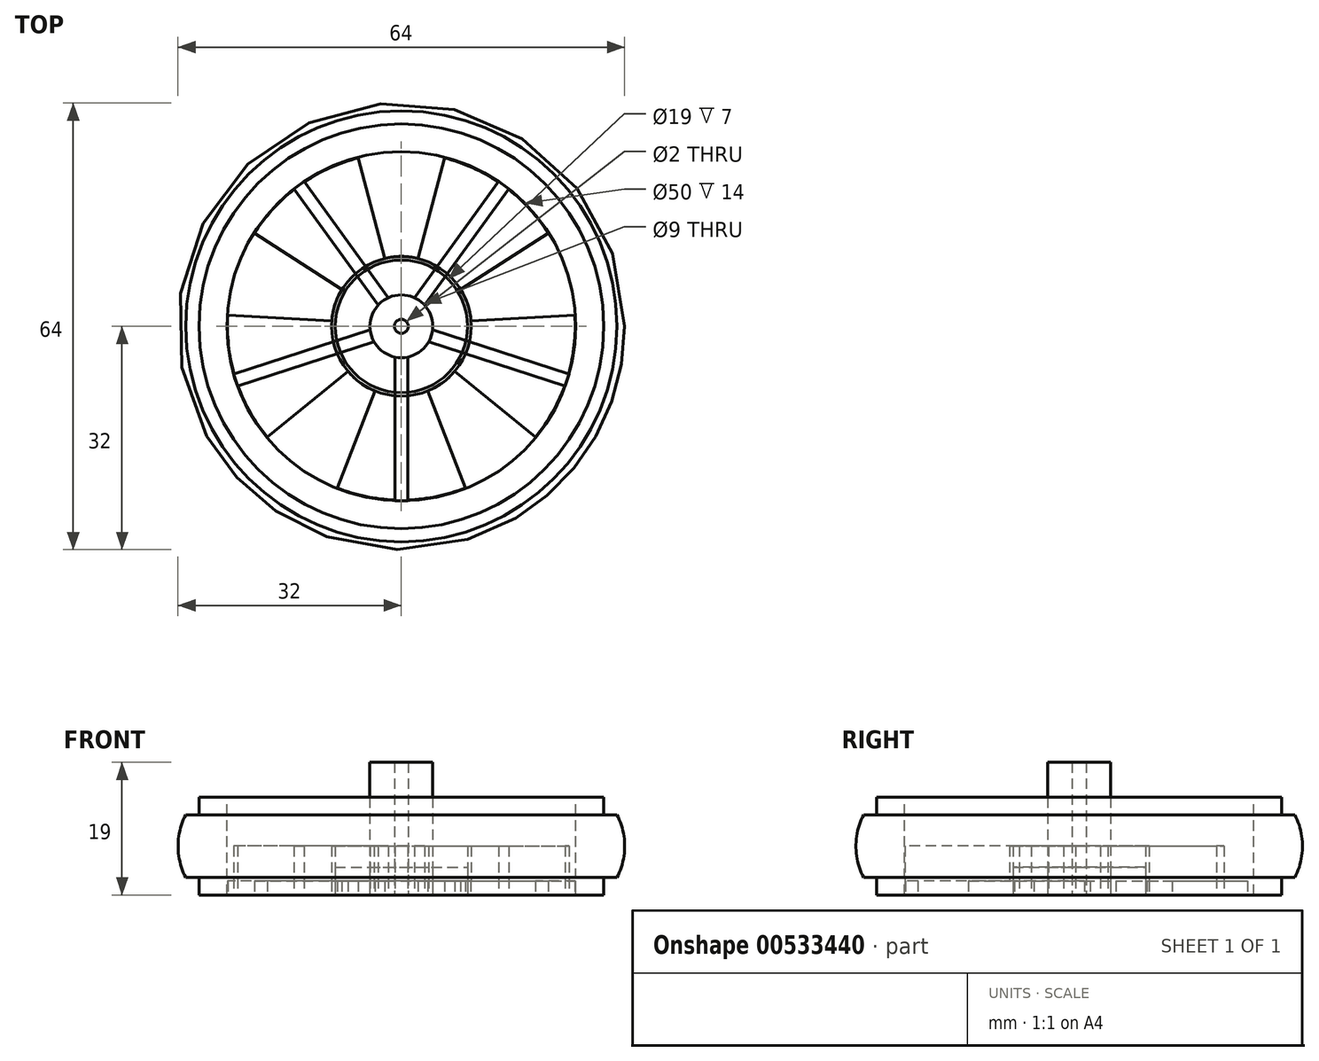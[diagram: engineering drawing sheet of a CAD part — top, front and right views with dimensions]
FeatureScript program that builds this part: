
annotation { "Feature Type Name" : "Feature", "Feature Type Description" : "" }
export const myFeature = defineFeature(function(context is Context, id is Id, definition is map)
    precondition{}
    {
        {
            var Q0;
            Q0=qCreatedBy(makeId("Front.planeOp"),FACE);
            var sketch = newSketch(context, id + "F0", { "sketchPlane" : qUnion([Q0])});
            skLineSegment(sketch, "E0", {"start": v(0, 0) * mm, "end": v(25, 0) * mm});
            skLineSegment(sketch, "E1", {"start": v(25, 0) * mm, "end": v(25, 14) * mm});
            skLineSegment(sketch, "E2", {"start": v(25, 14) * mm, "end": v(29, 14) * mm});
            skLineSegment(sketch, "E3", {"start": v(25, 0) * mm, "end": v(29, 0) * mm});
            skArc(sketch, "E4", {"start": v(30.89, 2.5) * mm, "mid": v(32, 7) * mm, "end": v(30.89, 11.5) * mm});
            skLineSegment(sketch, "E5", {"start": v(0, 2) * mm, "end": v(25, 2) * mm});
            skLineSegment(sketch, "E6", {"start": v(0, 30.9) * mm, "end": v(0, -20.2) * mm, "construction": true});
            skLineSegment(sketch, "E7", {"start": v(29, 14) * mm, "end": v(29, 11.5) * mm});
            skLineSegment(sketch, "E8", {"start": v(29, 11.5) * mm, "end": v(30.89, 11.5) * mm});
            skLineSegment(sketch, "E9", {"start": v(29, 0) * mm, "end": v(29, 2.5) * mm});
            skLineSegment(sketch, "E10", {"start": v(29, 2.5) * mm, "end": v(30.89, 2.5) * mm});
            skSolve(sketch);
        }
        {
            var Q0;
            {var subQ1=sQuery(id+"F0.wireOp",EDGE,"E2");Q0=makeQuery(id+"F0.imprint","IMPRINT",FACE,{"disambiguationData":[TD([[makeQuery(id+"F0.imprint","IMPRINT",EDGE,{"derivedFrom":subQ1}),-1.0]])]});}
            var Q1;
            Q1=sQuery(id+"F0.wireOp",EDGE,"E6");
            revolve(context, id + "F1", {"entities" : qUnion([Q0]), "axis" : qUnion([Q1]), "revolveType" : RevolveType.FULL});
        }
        {
            var Q0;
            Q0=makeQuery(id+"F1.opRevolve","SWEPT_FACE",FACE,{"disambiguationData":[OSD([sQuery(id+"F0.wireOp",EDGE,"E3")])]});
            var sketch = newSketch(context, id + "F2", { "sketchPlane" : qUnion([Q0])});
            skCircle(sketch, "E11", {"center": v(0, 0) * mm, "radius": 24.91 * mm});
            skCircle(sketch, "E12", {"center": v(0, 0) * mm, "radius": 4.5 * mm});
            skCircle(sketch, "E13", {"center": v(0, 0) * mm, "radius": 1 * mm});
            skCircle(sketch, "E14", {"center": v(0, 0) * mm, "radius": 9.5 * mm});
            skCircle(sketch, "E15", {"center": v(0, 0) * mm, "radius": 10 * mm});
            skSolve(sketch);
        }
        {
            var Q0;
            Q0 = qSketchRegion(id + "F2", true);
            extrude(context, id + "F3", {"entities" : qUnion([Q0]), "oppositeDirection" : true, "depth" : 2 * mm, "offsetDistance" : 25 * mm});
        }
        {
            var Q0;
            Q0=makeQuery(id+"F2.imprint","IMPRINT",FACE,{"disambiguationData":[TD([[makeQuery(id+"F2.imprint","IMPRINT",EDGE,{"derivedFrom":sQuery(id+"F2.wireOp",EDGE,"E12")}),1.0]])]});
            extrude(context, id + "F4", {"entities" : qUnion([Q0]), "oppositeDirection" : true, "depth" : 19 * mm, "offsetDistance" : 25 * mm});
        }
        {
            var Q0;
            Q0=makeQuery(id+"F2.imprint","IMPRINT",FACE,{"disambiguationData":[TD([[makeQuery(id+"F2.imprint","IMPRINT",EDGE,{"derivedFrom":sQuery(id+"F2.wireOp",EDGE,"E14")}),-1.0]])]});
            extrude(context, id + "F5", {"entities" : qUnion([Q0]), "operationType" : NewBodyOperationType.ADD, "oppositeDirection" : true, "depth" : 7 * mm, "offsetDistance" : 25 * mm});
        }
        {
            var Q0;
            Q0=makeQuery(id+"F2.imprint","IMPRINT",FACE,{"disambiguationData":[TD([[makeQuery(id+"F2.imprint","IMPRINT",EDGE,{"derivedFrom":sQuery(id+"F2.wireOp",EDGE,"E12")}),-1.0]])]});
            extrude(context, id + "F6", {"entities" : qUnion([Q0]), "oppositeDirection" : true, "depth" : 4 * mm, "offsetDistance" : 25 * mm});
        }
        {
            var Q0;
            Q0=qCreatedBy(makeId("Top.planeOp"),FACE);
            var sketch = newSketch(context, id + "F7", { "sketchPlane" : qUnion([Q0])});
            skLineSegment(sketch, "E16.bottom", {"start": v(0, -4.4) * mm, "end": v(-0.9, -4.4) * mm});
            skLineSegment(sketch, "E16.top", {"start": v(0, -24.98) * mm, "end": v(-0.9, -24.98) * mm});
            skLineSegment(sketch, "E16.right", {"start": v(-0.9, -4.4) * mm, "end": v(-0.9, -24.98) * mm});
            skLineSegment(sketch, "E17.MirrorCS", {"start": v(0.9, -4.4) * mm, "end": v(0.9, -24.98) * mm});
            skLineSegment(sketch, "E18", {"start": v(0, -24.98) * mm, "end": v(0.9, -24.98) * mm});
            skLineSegment(sketch, "E19", {"start": v(0, -4.4) * mm, "end": v(0.9, -4.4) * mm});
            skLineSegment(sketch, "E20.1.0", {"start": v(3.91, -2.23) * mm, "end": v(23.48, -8.58) * mm});
            skLineSegment(sketch, "E20.1.1", {"start": v(4.47, -0.5) * mm, "end": v(24.04, -6.86) * mm});
            skLineSegment(sketch, "E20.1.2", {"start": v(4.2, -1.36) * mm, "end": v(4.47, -0.5) * mm});
            skLineSegment(sketch, "E20.1.3", {"start": v(4.2, -1.36) * mm, "end": v(3.91, -2.23) * mm});
            skLineSegment(sketch, "E20.1.4", {"start": v(23.76, -7.72) * mm, "end": v(24.04, -6.86) * mm});
            skLineSegment(sketch, "E20.1.5", {"start": v(23.76, -7.72) * mm, "end": v(23.48, -8.58) * mm});
            skLineSegment(sketch, "E20.2.0", {"start": v(3.33, 3.03) * mm, "end": v(15.42, 19.68) * mm});
            skLineSegment(sketch, "E20.2.1", {"start": v(1.86, 4.1) * mm, "end": v(13.95, 20.75) * mm});
            skLineSegment(sketch, "E20.2.2", {"start": v(2.6, 3.57) * mm, "end": v(1.86, 4.1) * mm});
            skLineSegment(sketch, "E20.2.3", {"start": v(2.6, 3.57) * mm, "end": v(3.33, 3.03) * mm});
            skLineSegment(sketch, "E20.2.4", {"start": v(14.68, 20.21) * mm, "end": v(13.95, 20.75) * mm});
            skLineSegment(sketch, "E20.2.5", {"start": v(14.68, 20.21) * mm, "end": v(15.42, 19.68) * mm});
            skPoint(sketch, "E20.center", {"position": v(0, 0) * mm});
            skLineSegment(sketch, "E21.2.3.0", {"start": v(-1.86, 4.1) * mm, "end": v(-13.95, 20.75) * mm});
            skLineSegment(sketch, "E21.3.3.0", {"start": v(-3.33, 3.03) * mm, "end": v(-15.42, 19.68) * mm});
            skLineSegment(sketch, "E21.6.3.0", {"start": v(-2.6, 3.57) * mm, "end": v(-3.33, 3.03) * mm});
            skLineSegment(sketch, "E21.9.3.0", {"start": v(-2.6, 3.57) * mm, "end": v(-1.86, 4.1) * mm});
            skLineSegment(sketch, "E21.12.3.0", {"start": v(-14.68, 20.21) * mm, "end": v(-15.42, 19.68) * mm});
            skLineSegment(sketch, "E21.15.3.0", {"start": v(-14.68, 20.21) * mm, "end": v(-13.95, 20.75) * mm});
            skLineSegment(sketch, "E21.2.4.0", {"start": v(-4.47, -0.5) * mm, "end": v(-24.04, -6.86) * mm});
            skLineSegment(sketch, "E21.3.4.0", {"start": v(-3.91, -2.23) * mm, "end": v(-23.48, -8.58) * mm});
            skLineSegment(sketch, "E21.6.4.0", {"start": v(-4.2, -1.36) * mm, "end": v(-3.91, -2.23) * mm});
            skLineSegment(sketch, "E21.9.4.0", {"start": v(-4.2, -1.36) * mm, "end": v(-4.47, -0.5) * mm});
            skLineSegment(sketch, "E21.12.4.0", {"start": v(-23.76, -7.72) * mm, "end": v(-23.48, -8.58) * mm});
            skLineSegment(sketch, "E21.15.4.0", {"start": v(-23.76, -7.72) * mm, "end": v(-24.04, -6.86) * mm});
            skSolve(sketch);
        }
        {
            var Q0;
            Q0=makeQuery(id+"F7.imprint","IMPRINT",FACE,{"disambiguationData":[TD([[makeQuery(id+"F7.imprint","IMPRINT",EDGE,{"derivedFrom":sQuery(id+"F7.wireOp",EDGE,"E16.bottom")}),1.0]])]});
            var Q1;
            Q1=makeQuery(id+"F7.imprint","IMPRINT",FACE,{"disambiguationData":[TD([[makeQuery(id+"F7.imprint","IMPRINT",EDGE,{"derivedFrom":sQuery(id+"F7.wireOp",EDGE,"E20.1.0")}),1.0]])]});
            var Q2;
            Q2=makeQuery(id+"F7.imprint","IMPRINT",FACE,{"disambiguationData":[TD([[makeQuery(id+"F7.imprint","IMPRINT",EDGE,{"derivedFrom":sQuery(id+"F7.wireOp",EDGE,"E21.2.4.0")}),1.0]])]});
            var Q3;
            Q3=makeQuery(id+"F7.imprint","IMPRINT",FACE,{"disambiguationData":[TD([[makeQuery(id+"F7.imprint","IMPRINT",EDGE,{"derivedFrom":sQuery(id+"F7.wireOp",EDGE,"E21.2.3.0")}),1.0]])]});
            var Q4;
            Q4=makeQuery(id+"F7.imprint","IMPRINT",FACE,{"disambiguationData":[TD([[makeQuery(id+"F7.imprint","IMPRINT",EDGE,{"derivedFrom":sQuery(id+"F7.wireOp",EDGE,"E20.2.0")}),1.0]])]});
            extrude(context, id + "F8", {"entities" : qUnion([Q0, Q1, Q2, Q3, Q4]), "depth" : 7 * mm, "offsetDistance" : 25 * mm});
        }
        {
            var Q0;
            {var subQ0=sQuery(id+"F2.wireOp",EDGE,"E15");Q0=makeQuery(id+"F5.boolean.opBoolean","MERGE",FACE,{"derivedFrom":[makeQuery(id+"F3.opExtrude","CAP_FACE",FACE,{"disambiguationData":[OSD([sQuery(id+"F2.wireOp",EDGE,"E11"),subQ0])],"isStart":true}),makeQuery(id+"F5.opExtrude","CAP_FACE",FACE,{"disambiguationData":[OSD([sQuery(id+"F2.wireOp",EDGE,"E14"),subQ0])],"isStart":true})]});}
            var sketch = newSketch(context, id + "F9", { "sketchPlane" : qUnion([Q0])});
            skSolve(sketch);
        }
        {
            var Q0;
            Q0=makeQuery(id+"F9.imprint","IMPRINT",FACE,{"disambiguationData":[TD([[makeQuery(id+"F9.imprint","IMPRINT",EDGE,{"derivedFrom":makeQuery(id+"F3.opExtrude","CAP_EDGE",EDGE,{"disambiguationData":[OSD([sQuery(id+"F2.wireOp",EDGE,"E11")])],"isStart":true})}),1.0]])]});
            var sketch = newSketch(context, id + "F10", { "sketchPlane" : qUnion([Q0])});
            skLineSegment(sketch, "E22", {"start": v(-2.38, -9.71) * mm, "end": v(-6.19, -24.17) * mm});
            skLineSegment(sketch, "E23", {"start": v(0, -4) * mm, "end": v(0, -28.61) * mm, "construction": true});
            skLineSegment(sketch, "E24.MirrorCS", {"start": v(2.38, -9.71) * mm, "end": v(6.19, -24.17) * mm});
            skArc(sketch, "E25", {"start": v(-2.38, -9.71) * mm, "mid": v(0, -10.01) * mm, "end": v(2.38, -9.71) * mm});
            skArc(sketch, "E26", {"start": v(-6.19, -24.17) * mm, "mid": v(0, -24.94) * mm, "end": v(6.19, -24.17) * mm});
            skArc(sketch, "E27.1.0", {"start": v(8.5, -5.26) * mm, "mid": v(9.52, -3.1) * mm, "end": v(9.97, -0.74) * mm});
            skLineSegment(sketch, "E27.1.1", {"start": v(8.5, -5.26) * mm, "end": v(21.07, -13.35) * mm});
            skLineSegment(sketch, "E27.1.2", {"start": v(9.97, -0.74) * mm, "end": v(24.9, -1.58) * mm});
            skArc(sketch, "E27.1.3", {"start": v(21.07, -13.35) * mm, "mid": v(23.72, -7.7) * mm, "end": v(24.9, -1.58) * mm});
            skArc(sketch, "E27.2.0", {"start": v(7.63, 6.46) * mm, "mid": v(5.89, 8.1) * mm, "end": v(3.79, 9.26) * mm});
            skLineSegment(sketch, "E27.2.1", {"start": v(7.63, 6.46) * mm, "end": v(19.2, 15.91) * mm});
            skLineSegment(sketch, "E27.2.2", {"start": v(3.79, 9.26) * mm, "end": v(9.2, 23.19) * mm});
            skArc(sketch, "E27.2.3", {"start": v(19.2, 15.91) * mm, "mid": v(14.66, 20.18) * mm, "end": v(9.2, 23.19) * mm});
            skArc(sketch, "E27.3.0", {"start": v(-3.79, 9.26) * mm, "mid": v(-5.89, 8.1) * mm, "end": v(-7.63, 6.46) * mm});
            skLineSegment(sketch, "E27.3.1", {"start": v(-3.79, 9.26) * mm, "end": v(-9.2, 23.19) * mm});
            skLineSegment(sketch, "E27.3.2", {"start": v(-7.63, 6.46) * mm, "end": v(-19.2, 15.91) * mm});
            skArc(sketch, "E27.3.3", {"start": v(-9.2, 23.19) * mm, "mid": v(-14.66, 20.18) * mm, "end": v(-19.2, 15.91) * mm});
            skArc(sketch, "E27.4.0", {"start": v(-9.97, -0.74) * mm, "mid": v(-9.52, -3.1) * mm, "end": v(-8.5, -5.26) * mm});
            skLineSegment(sketch, "E27.4.1", {"start": v(-9.97, -0.74) * mm, "end": v(-24.9, -1.58) * mm});
            skLineSegment(sketch, "E27.4.2", {"start": v(-8.5, -5.26) * mm, "end": v(-21.07, -13.35) * mm});
            skArc(sketch, "E27.4.3", {"start": v(-24.9, -1.58) * mm, "mid": v(-23.72, -7.7) * mm, "end": v(-21.07, -13.35) * mm});
            skPoint(sketch, "E27.center", {"position": v(0, 0) * mm});
            skCircle(sketch, "E28.0", {"center": v(0, 0) * mm, "radius": 10 * mm});
            skSolve(sketch);
        }
        {
            var Q0;
            {var subQ0=sQuery(id+"F10.wireOp",EDGE,"E27.2.0");Q0=makeQuery(id+"F10.imprint","IMPRINT",FACE,{"disambiguationData":[TD([[makeQuery(id+"F10.imprint","IMPRINT",EDGE,{"derivedFrom":subQ0}),-1.0]])]});}
            var Q1;
            {var subQ0=sQuery(id+"F10.wireOp",EDGE,"E27.3.0");Q1=makeQuery(id+"F10.imprint","IMPRINT",FACE,{"disambiguationData":[TD([[makeQuery(id+"F10.imprint","IMPRINT",EDGE,{"derivedFrom":subQ0}),-1.0]])]});}
            var Q2;
            {var subQ0=sQuery(id+"F10.wireOp",EDGE,"E27.4.0");Q2=makeQuery(id+"F10.imprint","IMPRINT",FACE,{"disambiguationData":[TD([[makeQuery(id+"F10.imprint","IMPRINT",EDGE,{"derivedFrom":subQ0}),-1.0]])]});}
            var Q3;
            {var subQ1=sQuery(id+"F10.wireOp",EDGE,"E25");Q3=makeQuery(id+"F10.imprint","IMPRINT",FACE,{"disambiguationData":[TD([[makeQuery(id+"F10.imprint","IMPRINT",EDGE,{"derivedFrom":subQ1}),-1.0]])]});}
            var Q4;
            {var subQ0=sQuery(id+"F10.wireOp",EDGE,"E27.1.0");Q4=makeQuery(id+"F10.imprint","IMPRINT",FACE,{"disambiguationData":[TD([[makeQuery(id+"F10.imprint","IMPRINT",EDGE,{"derivedFrom":subQ0}),-1.0]])]});}
            extrude(context, id + "F11", {"entities" : qUnion([Q0, Q1, Q2, Q3, Q4]), "operationType" : NewBodyOperationType.REMOVE, "endBound" : BoundingType.THROUGH_ALL, "oppositeDirection" : true, "depth" : 25 * mm, "offsetDistance" : 25 * mm});
        }
    });
